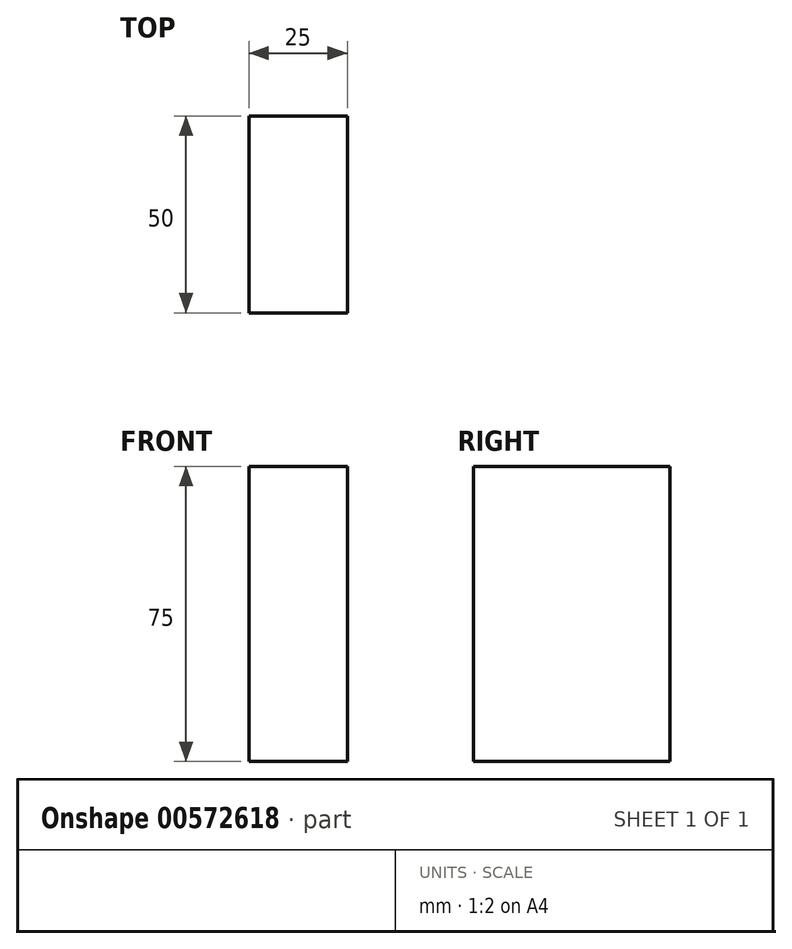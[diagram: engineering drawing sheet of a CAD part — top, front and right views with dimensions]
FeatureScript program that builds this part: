
annotation { "Feature Type Name" : "Feature", "Feature Type Description" : "" }
export const myFeature = defineFeature(function(context is Context, id is Id, definition is map)
    precondition{}
    {
        {
            var Q0;
            Q0=qCreatedBy(makeId("Top.planeOp"),FACE);
            var sketch = newSketch(context, id + "F0", { "sketchPlane" : qUnion([Q0])});
            skLineSegment(sketch, "E0.bottom", {"start": v(-34.32, 51.84) * mm, "end": v(-9.32, 51.84) * mm});
            skLineSegment(sketch, "E0.top", {"start": v(-34.32, 1.84) * mm, "end": v(-9.32, 1.84) * mm});
            skLineSegment(sketch, "E0.left", {"start": v(-34.32, 51.84) * mm, "end": v(-34.32, 1.84) * mm});
            skLineSegment(sketch, "E0.right", {"start": v(-9.32, 51.84) * mm, "end": v(-9.32, 1.84) * mm});
            skSolve(sketch);
        }
        {
            var Q0;
            Q0 = qSketchRegion(id + "F0", true);
            extrude(context, id + "F1", {"entities" : qUnion([Q0]), "depth" : 75 * mm, "offsetDistance" : 25 * mm});
        }
    });
